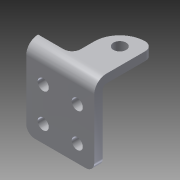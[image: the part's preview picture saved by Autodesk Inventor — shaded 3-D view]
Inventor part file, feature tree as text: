
AUTODESK INVENTOR PART (.ipt)
format: ipt  version: 2014 (Build 180170000, 170)  size: 158,720 bytes
history: native  units: in
note: dims shown in document units (in); Inventor stores cm internally (conversion verified against a paired STEP export)
features: sheet_metal_op x4, sketch x3, other x2, extrude x1, fillet x1
ambient origin geometry x8: Origin, YZ Plane, XZ Plane, XY Plane, X Axis, Y Axis, Z Axis, Center Point
bodies: Solid1 (feature_tree)
feature tree (11):
  sheet_metal_op  "Face1"
  sheet_metal_op  "Flange1"
  extrude  "Extrusion1"  Depth=1.0in
  fillet  "Fillet1"  Radius=0.163in
  sketch  "Sketch1"  dims[d0=1.0in d1=1.0in d2=0.163in]
  other  "Plate1"
  sketch  "Sketch2"  dims[d3=0.25in]
  other  "Plate2"
  sheet_metal_op  "Bend1"
  sheet_metal_op  "Corner1"
  sketch  "Sketch3"  dims[d4=0.25in d5=0.7874in d7=0.5in d8=0.7874in d10=0.5in d13=0.125in d14=0.125in d15=0.0625in d16=0.25in d17=0.125in d18=0.875in d19=90.0deg d20=0.05in d21=0.5in d22=0.125in d23=0.125in d24=0.187in d25=0.25in d26=0.25in d27=0.375in d28=0.125in d29=1.0in d30=0.0in d31=0.125in]
